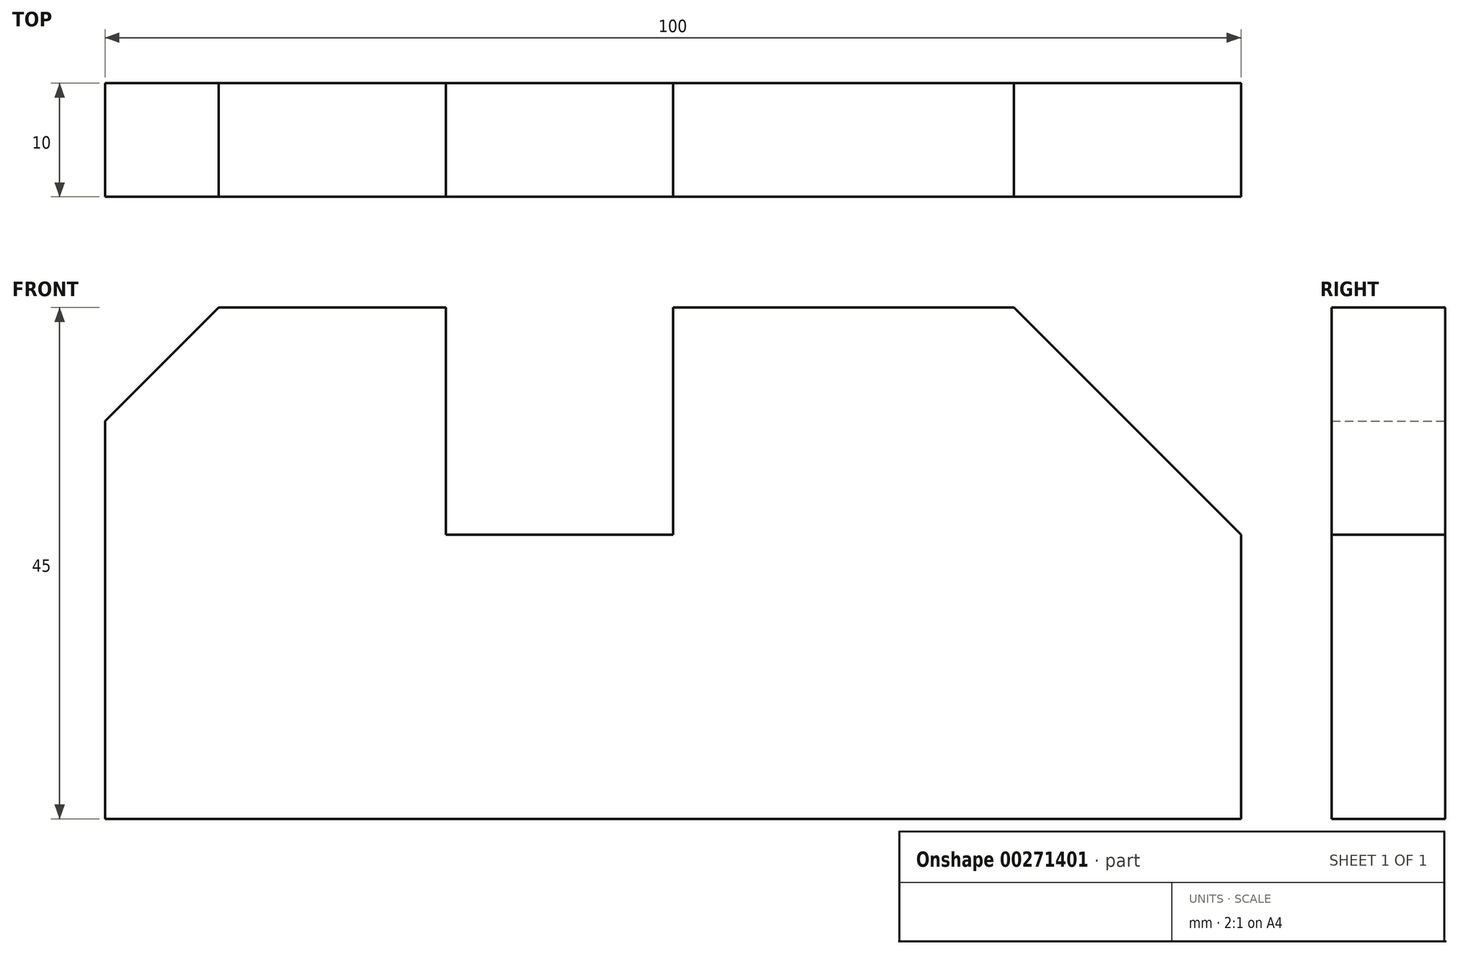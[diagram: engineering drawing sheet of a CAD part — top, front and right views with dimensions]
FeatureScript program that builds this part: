
annotation { "Feature Type Name" : "Feature", "Feature Type Description" : "" }
export const myFeature = defineFeature(function(context is Context, id is Id, definition is map)
    precondition{}
    {
        {
            var Q0;
            Q0=qCreatedBy(makeId("Front.planeOp"),FACE);
            var sketch = newSketch(context, id + "F0", { "sketchPlane" : qUnion([Q0])});
            skLineSegment(sketch, "E0", {"start": v(0, 0) * mm, "end": v(100, 0) * mm});
            skLineSegment(sketch, "E1", {"start": v(100, 0) * mm, "end": v(100, 25) * mm});
            skLineSegment(sketch, "E2", {"start": v(100, 25) * mm, "end": v(80, 45) * mm});
            skLineSegment(sketch, "E3", {"start": v(80, 45) * mm, "end": v(50, 45) * mm});
            skLineSegment(sketch, "E4", {"start": v(50, 45) * mm, "end": v(50, 25) * mm});
            skLineSegment(sketch, "E5", {"start": v(50, 25) * mm, "end": v(30, 25) * mm});
            skLineSegment(sketch, "E6", {"start": v(30, 25) * mm, "end": v(30, 45) * mm});
            skLineSegment(sketch, "E7", {"start": v(0, 35) * mm, "end": v(0, 0) * mm});
            skLineSegment(sketch, "E8", {"start": v(0, 35) * mm, "end": v(10, 45) * mm});
            skLineSegment(sketch, "E9", {"start": v(10, 45) * mm, "end": v(30, 45) * mm});
            skSolve(sketch);
        }
        {
            var Q0;
            Q0 = qSketchRegion(id + "F0", true);
            extrude(context, id + "F1", {"entities" : qUnion([Q0]), "depth" : 10 * mm});
        }
    });
